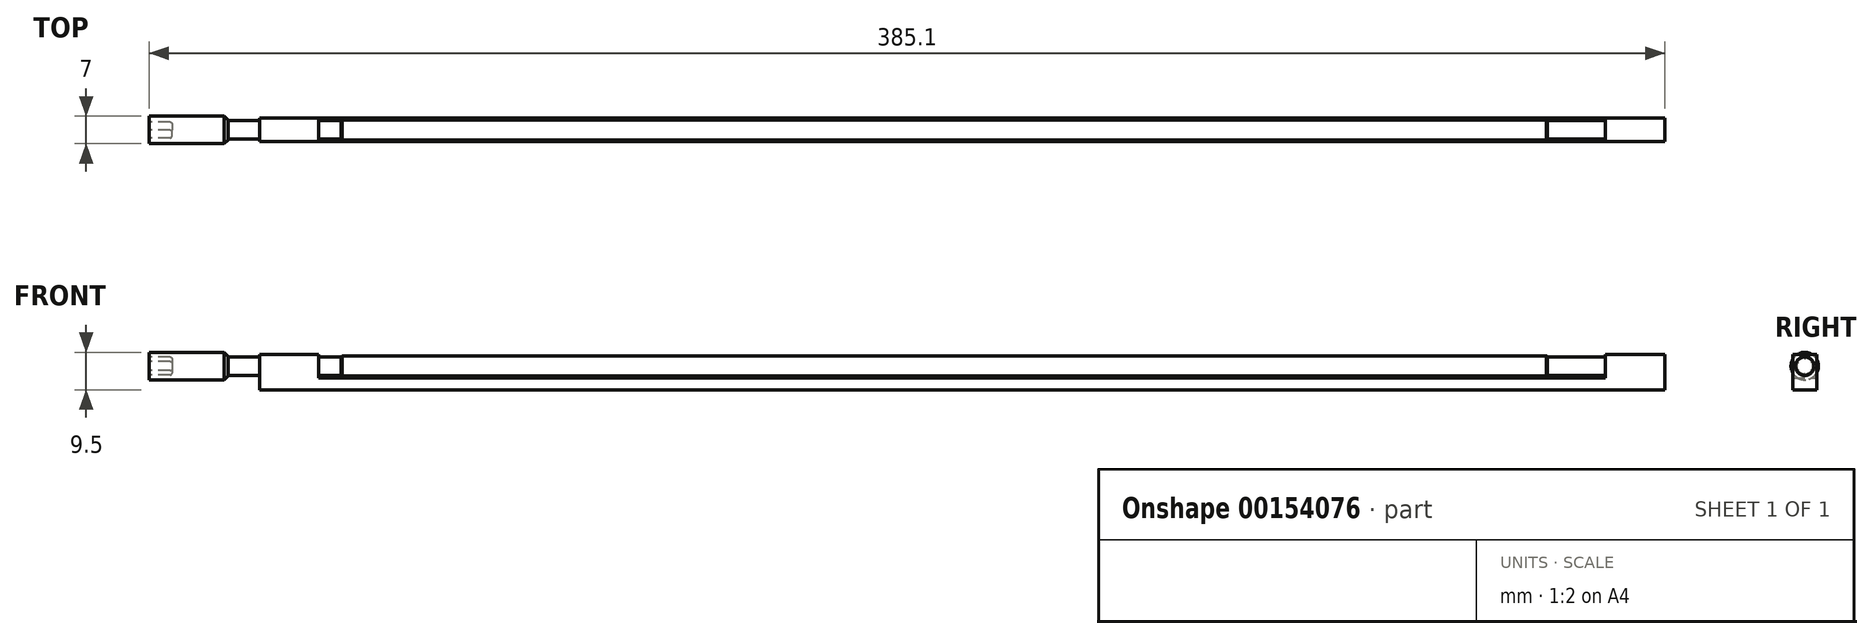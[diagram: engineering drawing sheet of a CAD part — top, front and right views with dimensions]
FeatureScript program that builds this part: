
annotation { "Feature Type Name" : "Feature", "Feature Type Description" : "" }
export const myFeature = defineFeature(function(context is Context, id is Id, definition is map)
    precondition{}
    {
        {
            var Q0;
            Q0=qCreatedBy(makeId("Front.planeOp"),FACE);
            var sketch = newSketch(context, id + "F0", { "sketchPlane" : qUnion([Q0])});
            skLineSegment(sketch, "E0.bottom", {"start": v(0, 0) * mm, "end": v(357, 0) * mm});
            skLineSegment(sketch, "E0.top", {"start": v(0, 3) * mm, "end": v(357, 3) * mm});
            skLineSegment(sketch, "E0.left", {"start": v(0, 0) * mm, "end": v(0, 3) * mm});
            skLineSegment(sketch, "E0.right", {"start": v(357, 0) * mm, "end": v(357, 3) * mm});
            skSolve(sketch);
        }
        {
            var Q0;
            Q0 = qSketchRegion(id + "F0", true);
            extrude(context, id + "F1", {"entities" : qUnion([Q0]), "endBound" : BoundingType.SYMMETRIC, "depth" : 6 * mm});
        }
        {
            var Q0;
            Q0=makeQuery(id+"F1.opExtrude","SWEPT_FACE",FACE,{"disambiguationData":[OSD([sQuery(id+"F0.wireOp",EDGE,"E0.right")])]});
            var sketch = newSketch(context, id + "F2", { "sketchPlane" : qUnion([Q0])});
            skLineSegment(sketch, "E1", {"start": v(3, 3) * mm, "end": v(-3, 3) * mm});
            skLineSegment(sketch, "E2", {"start": v(-3, 3) * mm, "end": v(-3, 9) * mm});
            skLineSegment(sketch, "E3", {"start": v(-3, 9) * mm, "end": v(3, 9) * mm});
            skLineSegment(sketch, "E4", {"start": v(3, 9) * mm, "end": v(3, 3) * mm});
            skSolve(sketch);
        }
        {
            var Q0;
            Q0 = qSketchRegion(id + "F2", true);
            extrude(context, id + "F3", {"entities" : qUnion([Q0]), "oppositeDirection" : true, "depth" : 15 * mm});
        }
        {
            var Q0;
            Q0=makeQuery(id+"F1.opExtrude","SWEPT_FACE",FACE,{"disambiguationData":[OSD([sQuery(id+"F0.wireOp",EDGE,"E0.left")])]});
            var sketch = newSketch(context, id + "F4", { "sketchPlane" : qUnion([Q0])});
            skLineSegment(sketch, "E5.0.0", {"start": v(3, 3) * mm, "end": v(3, 9) * mm});
            skLineSegment(sketch, "E5.0.1", {"start": v(3, 9) * mm, "end": v(-3, 9) * mm});
            skLineSegment(sketch, "E5.0.2", {"start": v(-3, 9) * mm, "end": v(-3, 3) * mm});
            skLineSegment(sketch, "E5.0.3", {"start": v(-3, 3) * mm, "end": v(3, 3) * mm});
            skSolve(sketch);
        }
        {
            var Q0;
            Q0 = qSketchRegion(id + "F4", true);
            extrude(context, id + "F5", {"entities" : qUnion([Q0]), "oppositeDirection" : true, "depth" : 15 * mm});
        }
        {
            var Q0;
            Q0=makeQuery(id+"F3.opExtrude","CAP_FACE",FACE,{"disambiguationData":[OSD([sQuery(id+"F2.wireOp",EDGE,"E1"),sQuery(id+"F2.wireOp",EDGE,"E2"),sQuery(id+"F2.wireOp",EDGE,"E3"),sQuery(id+"F2.wireOp",EDGE,"E4")])],"isStart":false});
            var sketch = newSketch(context, id + "F6", { "sketchPlane" : qUnion([Q0])});
            skCircle(sketch, "E6", {"center": v(0, 6) * mm, "radius": 2.36 * mm});
            skPoint(sketch, "E6.centerSnap0", {"position": v(3, 6) * mm});
            skSolve(sketch);
        }
        {
            var Q0;
            Q0 = qSketchRegion(id + "F6", true);
            extrude(context, id + "F7", {"entities" : qUnion([Q0]), "depth" : 14 * mm});
        }
        {
            var Q0;
            Q0=makeQuery(id+"F7.opExtrude","CAP_FACE",FACE,{"disambiguationData":[OSD([sQuery(id+"F6.wireOp",EDGE,"E6")])],"isStart":false});
            var sketch = newSketch(context, id + "F8", { "sketchPlane" : qUnion([Q0])});
            skCircle(sketch, "E7", {"center": v(0, 6) * mm, "radius": 2.56 * mm});
            skSolve(sketch);
        }
        {
            var Q0;
            Q0 = qSketchRegion(id + "F8", true);
            extrude(context, id + "F9", {"entities" : qUnion([Q0]), "operationType" : NewBodyOperationType.ADD, "depth" : 308 * mm});
        }
        {
            var Q0;
            Q0=makeQuery(id+"F9.opExtrude","CAP_FACE",FACE,{"disambiguationData":[OSD([sQuery(id+"F8.wireOp",EDGE,"E7")])],"isStart":false});
            var sketch = newSketch(context, id + "F10", { "sketchPlane" : qUnion([Q0])});
            skCircle(sketch, "E8", {"center": v(0, 6) * mm, "radius": 2.36 * mm});
            skSolve(sketch);
        }
        {
            var Q0;
            Q0 = qSketchRegion(id + "F10", true);
            extrude(context, id + "F11", {"entities" : qUnion([Q0]), "operationType" : NewBodyOperationType.ADD, "depth" : 28 * mm});
        }
        {
            var Q0;
            Q0 = qSketchRegion(id + "F6", true);
            extrude(context, id + "F12", {"entities" : qUnion([Q0]), "operationType" : NewBodyOperationType.ADD, "oppositeDirection" : true, "depth" : 15.1 * mm});
        }
        {
            var Q0;
            Q0=makeQuery(id+"F11.opExtrude","CAP_FACE",FACE,{"disambiguationData":[OSD([sQuery(id+"F10.wireOp",EDGE,"E8")])],"isStart":false});
            var sketch = newSketch(context, id + "F13", { "sketchPlane" : qUnion([Q0])});
            skCircle(sketch, "E9", {"center": v(0, 6) * mm, "radius": 3.5 * mm});
            skSolve(sketch);
        }
        {
            var Q0;
            Q0 = qSketchRegion(id + "F13", true);
            extrude(context, id + "F14", {"entities" : qUnion([Q0]), "depth" : 20 * mm});
        }
        {
            var Q0;
            Q0=makeQuery(id+"F14.opExtrude","CAP_EDGE",EDGE,{"disambiguationData":[OSD([sQuery(id+"F13.wireOp",EDGE,"E9")])],"isStart":true});
            var Q1;
            Q1=makeQuery(id+"F9.opExtrude","CAP_EDGE",EDGE,{"disambiguationData":[OSD([sQuery(id+"F8.wireOp",EDGE,"E7")])],"isStart":false});
            var Q2;
            Q2=makeQuery(id+"F9.opExtrude","CAP_EDGE",EDGE,{"disambiguationData":[OSD([sQuery(id+"F8.wireOp",EDGE,"E7")])],"isStart":true});
            chamfer(context, id + "F15", {"entities" : qUnion([Q0, Q1, Q2]), "width" : 1 * mm, "tangentPropagation" : true});
        }
        {
            var Q0;
            Q0=makeQuery(id+"F14.opExtrude","CAP_FACE",FACE,{"disambiguationData":[OSD([sQuery(id+"F13.wireOp",EDGE,"E9")])],"isStart":false});
            var sketch = newSketch(context, id + "F16", { "sketchPlane" : qUnion([Q0])});
            skCircle(sketch, "E10.cCircle", {"center": v(0, 6) * mm, "radius": 2 * mm, "construction": true});
            skLineSegment(sketch, "E10.0", {"start": v(2, 4.85) * mm, "end": v(0, 3.7) * mm});
            skLineSegment(sketch, "E10.1", {"start": v(0, 3.7) * mm, "end": v(-2, 4.85) * mm});
            skLineSegment(sketch, "E10.2", {"start": v(-2, 4.85) * mm, "end": v(-2, 7.15) * mm});
            skLineSegment(sketch, "E10.3", {"start": v(-2, 7.15) * mm, "end": v(0, 8.3) * mm});
            skLineSegment(sketch, "E10.4", {"start": v(0, 8.3) * mm, "end": v(2, 7.15) * mm});
            skLineSegment(sketch, "E10.5", {"start": v(2, 7.15) * mm, "end": v(2, 4.85) * mm});
            skPoint(sketch, "E10.0.midPoint", {"position": v(1, 4.27) * mm});
            skSolve(sketch);
        }
        {
            var Q0;
            Q0 = qSketchRegion(id + "F16", true);
            extrude(context, id + "F17", {"entities" : qUnion([Q0]), "operationType" : NewBodyOperationType.REMOVE, "oppositeDirection" : true, "depth" : 5.8 * mm});
        }
        {
            var Q0;
            Q0=makeQuery(id+"F17.boolean.opBoolean","COPY",FACE,{"derivedFrom":makeQuery(id+"F17.opExtrude","CAP_FACE",FACE,{"disambiguationData":[OSD([sQuery(id+"F16.wireOp",EDGE,"E10.0"),sQuery(id+"F16.wireOp",EDGE,"E10.1"),sQuery(id+"F16.wireOp",EDGE,"E10.2"),sQuery(id+"F16.wireOp",EDGE,"E10.3"),sQuery(id+"F16.wireOp",EDGE,"E10.4"),sQuery(id+"F16.wireOp",EDGE,"E10.5")])],"isStart":false})});
            fillet(context, id + "F18", {"entities" : qUnion([Q0]), "radius" : 0.5 * mm, "tangentPropagation" : true, "allowEdgeOverflow" : false});
        }
        {
            var Q0;
            Q0=makeQuery(id+"F1.opExtrude","SWEPT_BODY",BODY,{"disambiguationData":[OSD([sQuery(id+"F0.wireOp",EDGE,"E0.bottom"),sQuery(id+"F0.wireOp",EDGE,"E0.top"),sQuery(id+"F0.wireOp",EDGE,"E0.left"),sQuery(id+"F0.wireOp",EDGE,"E0.right")])]});
            var Q1;
            Q1=makeQuery(id+"F3.opExtrude","SWEPT_BODY",BODY,{"disambiguationData":[OSD([sQuery(id+"F2.wireOp",EDGE,"E1"),sQuery(id+"F2.wireOp",EDGE,"E2"),sQuery(id+"F2.wireOp",EDGE,"E3"),sQuery(id+"F2.wireOp",EDGE,"E4")])]});
            var Q2;
            Q2=makeQuery(id+"F5.opExtrude","SWEPT_BODY",BODY,{"disambiguationData":[OSD([sQuery(id+"F4.wireOp",EDGE,"E5.0.0"),sQuery(id+"F4.wireOp",EDGE,"E5.0.1"),sQuery(id+"F4.wireOp",EDGE,"E5.0.2"),sQuery(id+"F4.wireOp",EDGE,"E5.0.3")])]});
            var Q3;
            Q3=makeQuery(id+"F7.opExtrude","SWEPT_BODY",BODY,{"disambiguationData":[OSD([sQuery(id+"F6.wireOp",EDGE,"E6")])]});
            var Q4;
            Q4=makeQuery(id+"F14.opExtrude","SWEPT_BODY",BODY,{"disambiguationData":[OSD([sQuery(id+"F13.wireOp",EDGE,"E9")])]});
            booleanBodies(context, id + "F19", {"operationType" : BooleanOperationType.UNION, "tools" : qUnion([Q0, Q1, Q2, Q3, Q4])});
        }
    });
